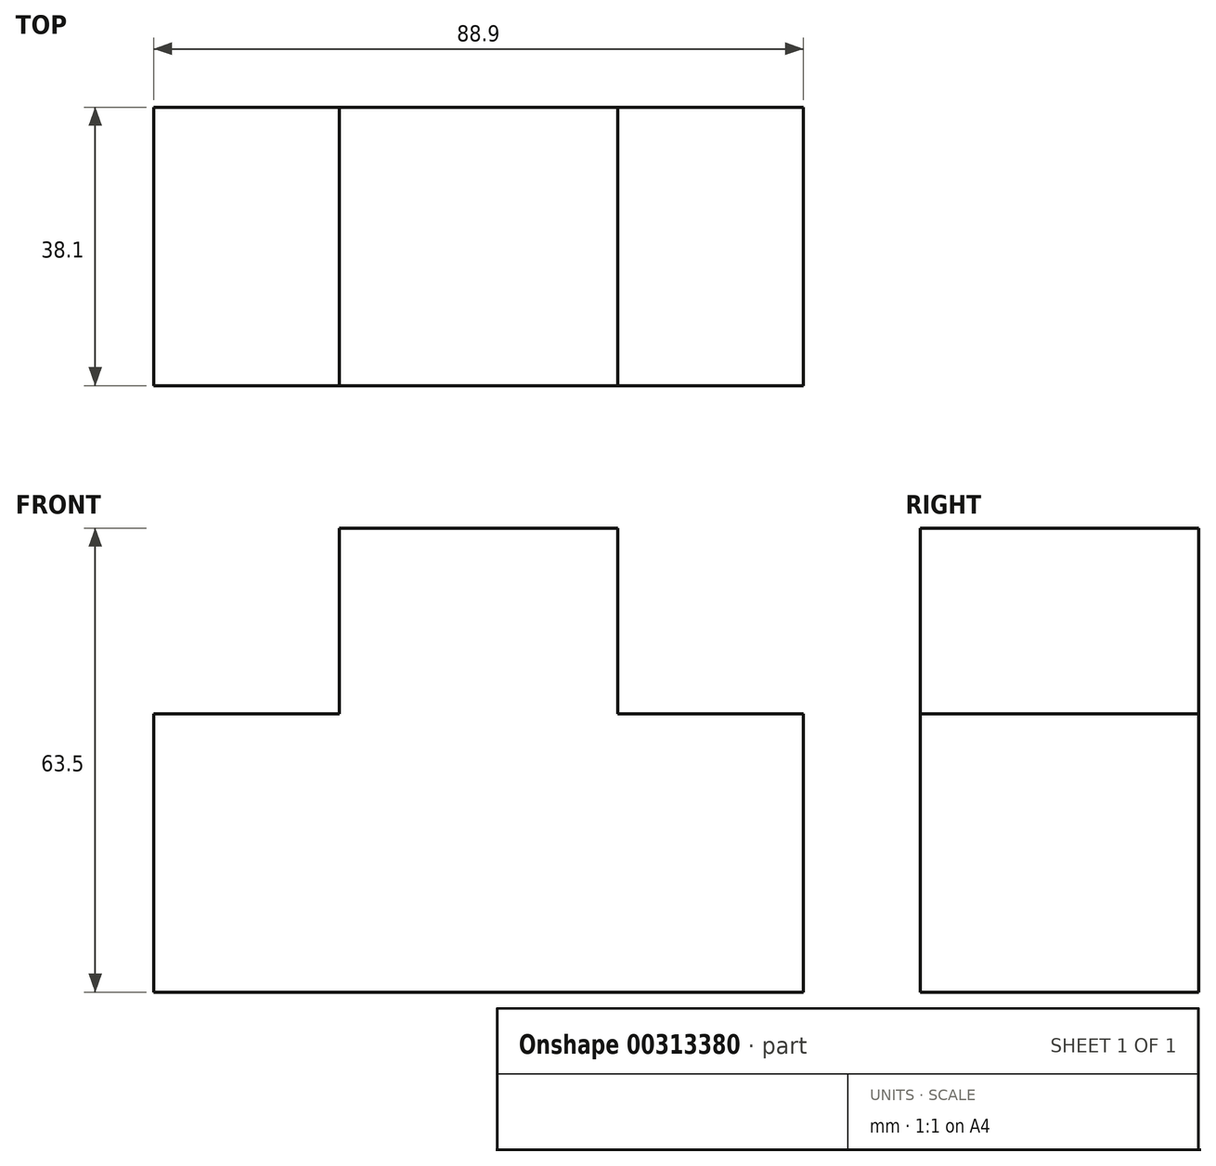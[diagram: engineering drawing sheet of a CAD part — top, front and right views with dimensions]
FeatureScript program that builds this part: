
annotation { "Feature Type Name" : "Feature", "Feature Type Description" : "" }
export const myFeature = defineFeature(function(context is Context, id is Id, definition is map)
    precondition{}
    {
        {
            var Q0;
            Q0=qCreatedBy(makeId("Front.planeOp"),FACE);
            var sketch = newSketch(context, id + "F0", { "sketchPlane" : qUnion([Q0])});
            skLineSegment(sketch, "E0", {"start": v(-45.3, -19.14) * mm, "end": v(43.6, -19.14) * mm});
            skLineSegment(sketch, "E1", {"start": v(43.6, -19.14) * mm, "end": v(43.6, 18.96) * mm});
            skLineSegment(sketch, "E2", {"start": v(43.6, 18.96) * mm, "end": v(18.2, 18.96) * mm});
            skLineSegment(sketch, "E3", {"start": v(18.2, 18.96) * mm, "end": v(18.2, 44.36) * mm});
            skLineSegment(sketch, "E4", {"start": v(18.2, 44.36) * mm, "end": v(-19.9, 44.36) * mm});
            skLineSegment(sketch, "E5", {"start": v(-19.9, 44.36) * mm, "end": v(-19.9, 18.96) * mm});
            skLineSegment(sketch, "E6", {"start": v(-19.9, 18.96) * mm, "end": v(-45.3, 18.96) * mm});
            skLineSegment(sketch, "E7", {"start": v(-45.3, 18.96) * mm, "end": v(-45.3, -19.14) * mm});
            skSolve(sketch);
        }
        {
            var Q0;
            Q0 = qSketchRegion(id + "F0", true);
            extrude(context, id + "F1", {"entities" : qUnion([Q0]), "depth" : 38.1 * mm});
        }
    });
